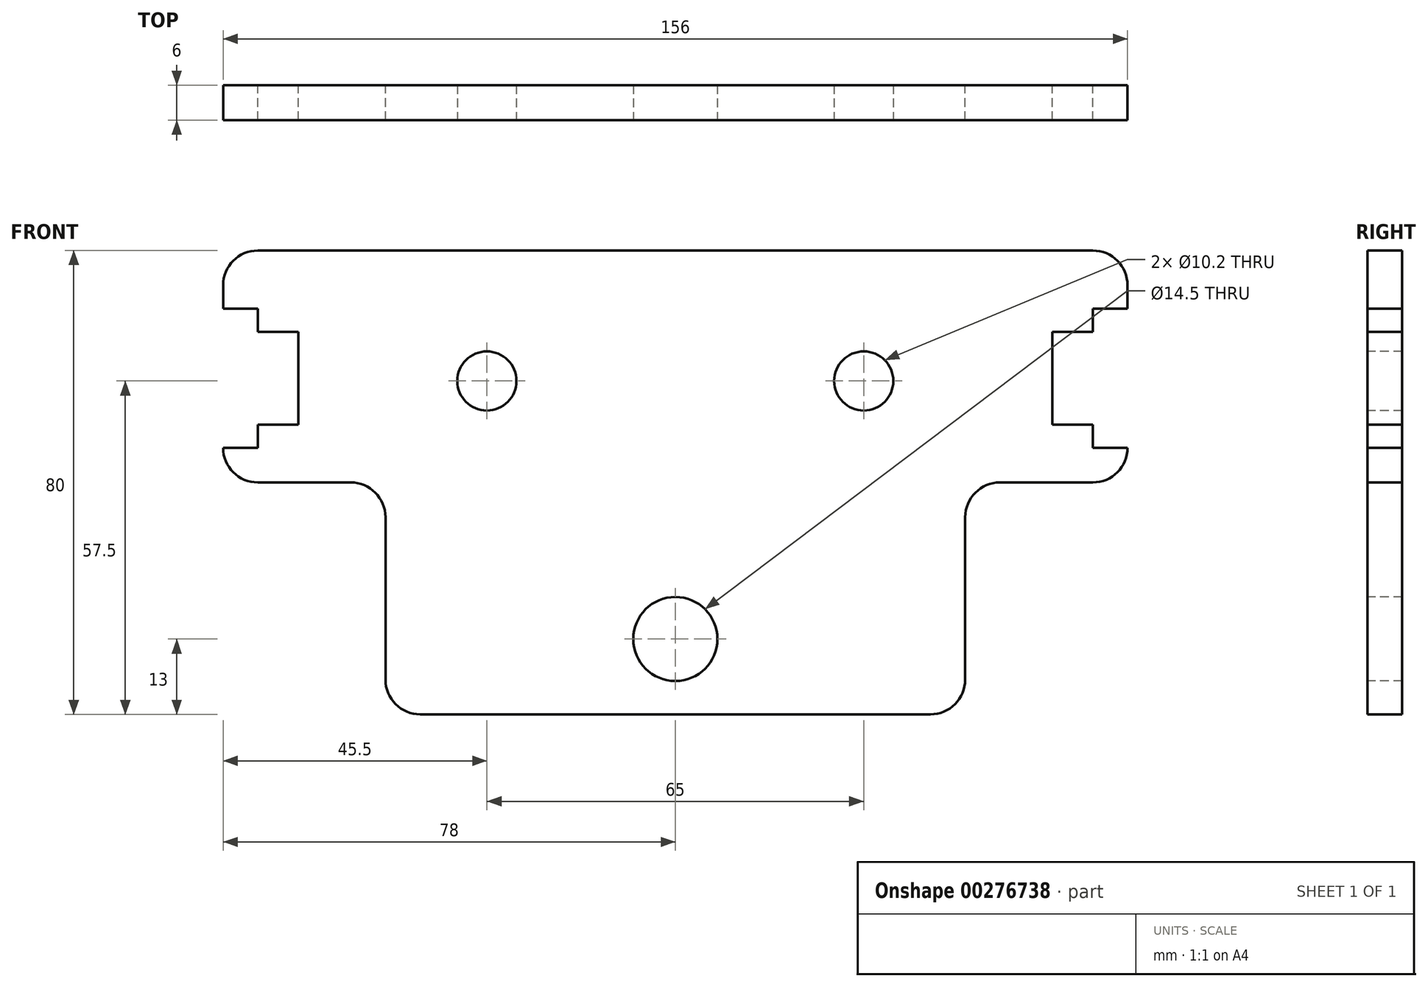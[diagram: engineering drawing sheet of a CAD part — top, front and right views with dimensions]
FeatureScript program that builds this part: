
annotation { "Feature Type Name" : "Feature", "Feature Type Description" : "" }
export const myFeature = defineFeature(function(context is Context, id is Id, definition is map)
    precondition{}
    {
        {
            var Q0;
            Q0=qCreatedBy(makeId("Front.planeOp"),FACE);
            var sketch = newSketch(context, id + "F0", { "sketchPlane" : qUnion([Q0])});
            skLineSegment(sketch, "E0", {"start": v(0, 0) * mm, "end": v(0, 80) * mm});
            skLineSegment(sketch, "E1", {"start": v(0, 80) * mm, "end": v(-78, 80) * mm});
            skLineSegment(sketch, "E2", {"start": v(-78, 80) * mm, "end": v(-78, 70) * mm});
            skLineSegment(sketch, "E3", {"start": v(-78, 70) * mm, "end": v(-72, 70) * mm});
            skLineSegment(sketch, "E4", {"start": v(-65, 66) * mm, "end": v(-65, 50) * mm});
            skLineSegment(sketch, "E5", {"start": v(-72, 46) * mm, "end": v(-78, 46) * mm});
            skLineSegment(sketch, "E6", {"start": v(-78, 46) * mm, "end": v(-78, 40) * mm});
            skLineSegment(sketch, "E7", {"start": v(-78, 40) * mm, "end": v(-50, 40) * mm});
            skLineSegment(sketch, "E8", {"start": v(-50, 40) * mm, "end": v(-50, 0) * mm});
            skLineSegment(sketch, "E9", {"start": v(-50, 0) * mm, "end": v(0, 0) * mm});
            skLineSegment(sketch, "E10.top", {"start": v(-65, 66) * mm, "end": v(-72, 66) * mm});
            skLineSegment(sketch, "E10.right", {"start": v(-72, 70) * mm, "end": v(-72, 66) * mm});
            skLineSegment(sketch, "E11.top", {"start": v(-65, 50) * mm, "end": v(-72, 50) * mm});
            skLineSegment(sketch, "E11.right", {"start": v(-72, 46) * mm, "end": v(-72, 50) * mm});
            skSolve(sketch);
        }
        {
            var Q0;
            Q0=makeQuery(id+"F0.imprint","IMPRINT",FACE,{"disambiguationData":[TD([[makeQuery(id+"F0.imprint","IMPRINT",EDGE,{"derivedFrom":sQuery(id+"F0.wireOp",EDGE,"E0")}),1.0]])]});
            extrude(context, id + "F1", {"entities" : qUnion([Q0]), "depth" : 6 * mm});
        }
        {
            var Q0;
            Q0=makeQuery(id+"F1.opExtrude","CAP_FACE",FACE,{"disambiguationData":[OSD([sQuery(id+"F0.wireOp",EDGE,"E0"),sQuery(id+"F0.wireOp",EDGE,"E1"),sQuery(id+"F0.wireOp",EDGE,"E2"),sQuery(id+"F0.wireOp",EDGE,"E3"),sQuery(id+"F0.wireOp",EDGE,"E4"),sQuery(id+"F0.wireOp",EDGE,"E5"),sQuery(id+"F0.wireOp",EDGE,"E6"),sQuery(id+"F0.wireOp",EDGE,"E7"),sQuery(id+"F0.wireOp",EDGE,"E8"),sQuery(id+"F0.wireOp",EDGE,"E9")])],"isStart":false});
            var sketch = newSketch(context, id + "F2", { "sketchPlane" : qUnion([Q0])});
            skCircle(sketch, "E12", {"center": v(-32.5, 57.5) * mm, "radius": 5.1 * mm});
            skSolve(sketch);
        }
        {
            var Q0;
            Q0=makeQuery(id+"F2.imprint","IMPRINT",FACE,{"disambiguationData":[TD([[makeQuery(id+"F2.imprint","IMPRINT",EDGE,{"derivedFrom":sQuery(id+"F2.wireOp",EDGE,"E12")}),1.0]])]});
            extrude(context, id + "F3", {"entities" : qUnion([Q0]), "operationType" : NewBodyOperationType.REMOVE, "oppositeDirection" : true, "depth" : 25 * mm});
        }
        {
            var Q0;
            Q0=makeQuery(id+"F1.opExtrude","CAP_FACE",FACE,{"disambiguationData":[OSD([sQuery(id+"F0.wireOp",EDGE,"E0"),sQuery(id+"F0.wireOp",EDGE,"E1"),sQuery(id+"F0.wireOp",EDGE,"E2"),sQuery(id+"F0.wireOp",EDGE,"E3"),sQuery(id+"F0.wireOp",EDGE,"E4"),sQuery(id+"F0.wireOp",EDGE,"E5"),sQuery(id+"F0.wireOp",EDGE,"E6"),sQuery(id+"F0.wireOp",EDGE,"E7"),sQuery(id+"F0.wireOp",EDGE,"E8"),sQuery(id+"F0.wireOp",EDGE,"E9")])],"isStart":false});
            var sketch = newSketch(context, id + "F4", { "sketchPlane" : qUnion([Q0])});
            skCircle(sketch, "E13", {"center": v(0, 13) * mm, "radius": 7.25 * mm});
            skSolve(sketch);
        }
        {
            var Q0;
            {var subQ0=sQuery(id+"F4.wireOp",EDGE,"E13");var subQ1=makeQuery(id+"F1.opExtrude","CAP_EDGE",EDGE,{"disambiguationData":[OSD([sQuery(id+"F0.wireOp",EDGE,"E0")])],"isStart":false});var subQ2=makeQuery(id+"F4.imprint","INTERSECT",VERTEX,{"disambiguationData":[OD(0.0)],"derivedFrom":[subQ1,subQ0]});Q0=makeQuery(id+"F4.imprint","IMPRINT",FACE,{"disambiguationData":[TD([[makeQuery(id+"F4.imprint","IMPRINT",EDGE,{"disambiguationData":[TD([[subQ2,1.0]])],"derivedFrom":subQ0}),1.0]])]});}
            extrude(context, id + "F5", {"entities" : qUnion([Q0]), "operationType" : NewBodyOperationType.REMOVE, "oppositeDirection" : true, "depth" : 25 * mm});
        }
        {
            var Q0;
            Q0=makeQuery(id+"F1.opExtrude","SWEPT_EDGE",EDGE,{"disambiguationData":[OSD([sQuery(id+"F0.wireOp",EDGE,"E1"),sQuery(id+"F0.wireOp",EDGE,"E2")])]});
            var Q1;
            Q1=makeQuery(id+"F1.opExtrude","SWEPT_EDGE",EDGE,{"disambiguationData":[OSD([sQuery(id+"F0.wireOp",EDGE,"E6"),sQuery(id+"F0.wireOp",EDGE,"E7")])]});
            var Q2;
            Q2=makeQuery(id+"F1.opExtrude","SWEPT_EDGE",EDGE,{"disambiguationData":[OSD([sQuery(id+"F0.wireOp",EDGE,"E8"),sQuery(id+"F0.wireOp",EDGE,"E9")])]});
            fillet(context, id + "F6", {"entities" : qUnion([Q0, Q1, Q2]), "radius" : 6 * mm, "tangentPropagation" : true, "allowEdgeOverflow" : false});
        }
        {
            var Q0;
            Q0=makeQuery(id+"F1.opExtrude","SWEPT_BODY",BODY,{"disambiguationData":[OSD([sQuery(id+"F0.wireOp",EDGE,"E0"),sQuery(id+"F0.wireOp",EDGE,"E1"),sQuery(id+"F0.wireOp",EDGE,"E2"),sQuery(id+"F0.wireOp",EDGE,"E3"),sQuery(id+"F0.wireOp",EDGE,"E4"),sQuery(id+"F0.wireOp",EDGE,"E5"),sQuery(id+"F0.wireOp",EDGE,"E6"),sQuery(id+"F0.wireOp",EDGE,"E7"),sQuery(id+"F0.wireOp",EDGE,"E8"),sQuery(id+"F0.wireOp",EDGE,"E9")])]});
            var Q1;
            {var subQ8=sQuery(id+"F0.wireOp",EDGE,"E1");var subQ9=sQuery(id+"F0.wireOp",EDGE,"E0");Q1=makeQuery(id+"F5.boolean.opBoolean","SPLIT",FACE,{"disambiguationData":[TD([makeQuery(id+"F1.opExtrude","SWEPT_FACE",FACE,{"disambiguationData":[OSD([subQ8])]})])],"derivedFrom":makeQuery(id+"F1.opExtrude","SWEPT_FACE",FACE,{"disambiguationData":[OSD([subQ9])]})});}
            mirror(context, id + "F7", {"operationType" : NewBodyOperationType.ADD, "entities" : qUnion([Q0]), "mirrorPlane" : qUnion([Q1])});
        }
        {
            var Q0;
            Q0=makeQuery(id+"F1.opExtrude","SWEPT_EDGE",EDGE,{"disambiguationData":[OSD([sQuery(id+"F0.wireOp",EDGE,"E7"),sQuery(id+"F0.wireOp",EDGE,"E8")])]});
            var Q1;
            Q1=makeQuery(id+"F7.opPattern","COPY",EDGE,{"derivedFrom":makeQuery(id+"F1.opExtrude","SWEPT_EDGE",EDGE,{"disambiguationData":[OSD([sQuery(id+"F0.wireOp",EDGE,"E7"),sQuery(id+"F0.wireOp",EDGE,"E8")])]}),"instanceName":"1"});
            fillet(context, id + "F8", {"entities" : qUnion([Q0, Q1]), "radius" : 6 * mm, "tangentPropagation" : true, "allowEdgeOverflow" : false});
        }
    });
